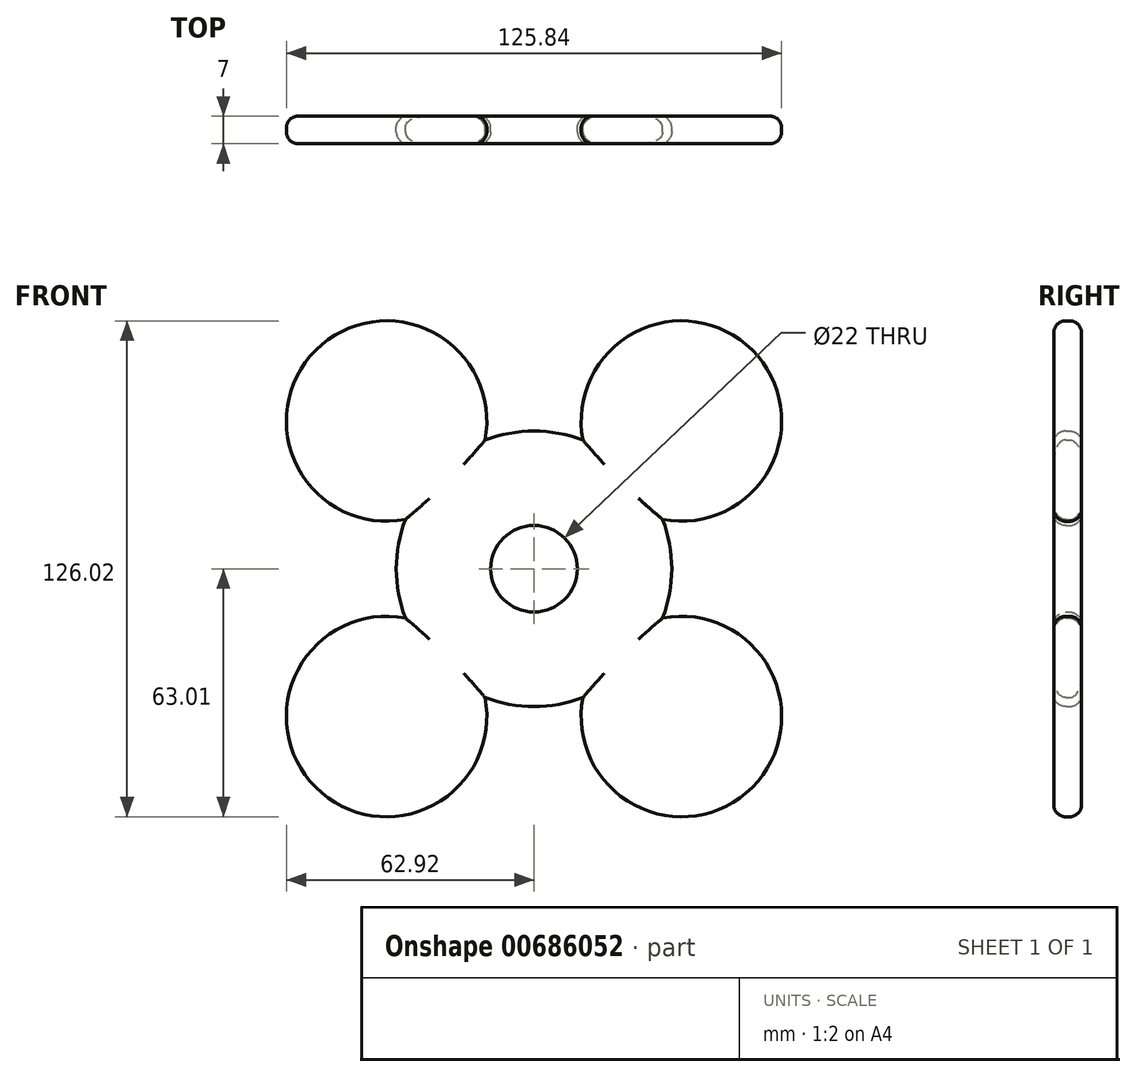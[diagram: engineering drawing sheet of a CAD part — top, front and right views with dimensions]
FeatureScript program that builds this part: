
annotation { "Feature Type Name" : "Feature", "Feature Type Description" : "" }
export const myFeature = defineFeature(function(context is Context, id is Id, definition is map)
    precondition{}
    {
        {
            var Q0;
            Q0=qCreatedBy(makeId("Front.planeOp"),FACE);
            var sketch = newSketch(context, id + "F0", { "sketchPlane" : qUnion([Q0])});
            skCircle(sketch, "E0", {"center": v(0, 0) * mm, "radius": 35 * mm});
            skCircle(sketch, "E1", {"center": v(0, 0) * mm, "radius": 11 * mm});
            skCircle(sketch, "E2", {"center": v(-37.45, 37.54) * mm, "radius": 25.47 * mm});
            skPoint(sketch, "E3.orphan", {"position": v(-74.9, 75.09) * mm});
            skLineSegment(sketch, "E4", {"start": v(0, 11) * mm, "end": v(0, -11) * mm});
            skLineSegment(sketch, "E5", {"start": v(-11, 0) * mm, "end": v(11, 0) * mm});
            skCircle(sketch, "E6.MirrorC", {"center": v(37.45, 37.54) * mm, "radius": 25.47 * mm});
            skLineSegment(sketch, "E7.MirrorCS", {"start": v(11, 0) * mm, "end": v(-11, 0) * mm});
            skCircle(sketch, "E8.MirrorC", {"center": v(37.45, -37.54) * mm, "radius": 25.47 * mm});
            skLineSegment(sketch, "E9.MirrorCS", {"start": v(0, -11) * mm, "end": v(0, 11) * mm});
            skCircle(sketch, "E10.MirrorC", {"center": v(-37.45, -37.54) * mm, "radius": 25.47 * mm});
            skSolve(sketch);
        }
        {
            var Q0;
            Q0 = qSketchRegion(id + "F0", true);
            extrude(context, id + "F1", {"entities" : qUnion([Q0]), "depth" : 7 * mm, "offsetDistance" : 25 * mm});
        }
        {
            var Q0;
            {var subQ0=sQuery(id+"F0.wireOp",EDGE,"E0");Q0=makeQuery(id+"F1.opExtrude","CAP_EDGE",EDGE,{"disambiguationData":[OSD([subQ0]),TDD([makeQuery(id+"F0.imprint","IMPRINT",EDGE,{"disambiguationData":[TD([[makeQuery(id+"F0.imprint","INTERSECT",VERTEX,{"disambiguationData":[OD(0.0)],"derivedFrom":[subQ0,sQuery(id+"F0.wireOp",EDGE,"E6.MirrorC")]}),-1.0]])],"derivedFrom":subQ0})])],"isStart":false});}
            var Q1;
            Q1=makeQuery(id+"F1.opExtrude","CAP_EDGE",EDGE,{"disambiguationData":[OSD([sQuery(id+"F0.wireOp",EDGE,"E2")])],"isStart":false});
            var Q2;
            Q2=makeQuery(id+"F1.opExtrude","CAP_EDGE",EDGE,{"disambiguationData":[OSD([sQuery(id+"F0.wireOp",EDGE,"E6.MirrorC")])],"isStart":false});
            var Q3;
            {var subQ0=sQuery(id+"F0.wireOp",EDGE,"E0");Q3=makeQuery(id+"F1.opExtrude","CAP_EDGE",EDGE,{"disambiguationData":[OSD([subQ0]),TDD([makeQuery(id+"F0.imprint","IMPRINT",EDGE,{"disambiguationData":[TD([[makeQuery(id+"F0.imprint","INTERSECT",VERTEX,{"disambiguationData":[OD(1.0)],"derivedFrom":[subQ0,sQuery(id+"F0.wireOp",EDGE,"E6.MirrorC")]}),1.0]])],"derivedFrom":subQ0})])],"isStart":false});}
            var Q4;
            Q4=makeQuery(id+"F1.opExtrude","CAP_EDGE",EDGE,{"disambiguationData":[OSD([sQuery(id+"F0.wireOp",EDGE,"E8.MirrorC")])],"isStart":false});
            var Q5;
            {var subQ0=sQuery(id+"F0.wireOp",EDGE,"E0");Q5=makeQuery(id+"F1.opExtrude","CAP_EDGE",EDGE,{"disambiguationData":[OSD([subQ0]),TDD([makeQuery(id+"F0.imprint","IMPRINT",EDGE,{"disambiguationData":[TD([[makeQuery(id+"F0.imprint","INTERSECT",VERTEX,{"disambiguationData":[OD(1.0)],"derivedFrom":[subQ0,sQuery(id+"F0.wireOp",EDGE,"E10.MirrorC")]}),-1.0]])],"derivedFrom":subQ0})])],"isStart":false});}
            var Q6;
            Q6=makeQuery(id+"F1.opExtrude","CAP_EDGE",EDGE,{"disambiguationData":[OSD([sQuery(id+"F0.wireOp",EDGE,"E10.MirrorC")])],"isStart":false});
            var Q7;
            {var subQ0=sQuery(id+"F0.wireOp",EDGE,"E0");Q7=makeQuery(id+"F1.opExtrude","CAP_EDGE",EDGE,{"disambiguationData":[OSD([subQ0]),TDD([makeQuery(id+"F0.imprint","IMPRINT",EDGE,{"disambiguationData":[TD([[makeQuery(id+"F0.imprint","INTERSECT",VERTEX,{"disambiguationData":[OD(1.0)],"derivedFrom":[subQ0,sQuery(id+"F0.wireOp",EDGE,"E2")]}),-1.0]])],"derivedFrom":subQ0})])],"isStart":false});}
            var Q8;
            Q8=makeQuery(id+"F1.opExtrude","CAP_FACE",FACE,{"disambiguationData":[OSD([sQuery(id+"F0.wireOp",EDGE,"E0"),sQuery(id+"F0.wireOp",EDGE,"E1"),sQuery(id+"F0.wireOp",EDGE,"E6.MirrorC"),sQuery(id+"F0.wireOp",EDGE,"E2"),sQuery(id+"F0.wireOp",EDGE,"E8.MirrorC"),sQuery(id+"F0.wireOp",EDGE,"E10.MirrorC")])],"isStart":true});
            var Q9;
            Q9=makeQuery(id+"F1.opExtrude","CAP_FACE",FACE,{"disambiguationData":[OSD([sQuery(id+"F0.wireOp",EDGE,"E0"),sQuery(id+"F0.wireOp",EDGE,"E1"),sQuery(id+"F0.wireOp",EDGE,"E6.MirrorC"),sQuery(id+"F0.wireOp",EDGE,"E2"),sQuery(id+"F0.wireOp",EDGE,"E8.MirrorC"),sQuery(id+"F0.wireOp",EDGE,"E10.MirrorC")])],"isStart":false});
            fillet(context, id + "F2", {"entities" : qUnion([Q0, Q1, Q2, Q3, Q4, Q5, Q6, Q7, Q8, Q9]), "radius" : 3 * mm, "tangentPropagation" : true, "allowEdgeOverflow" : false});
        }
    });
